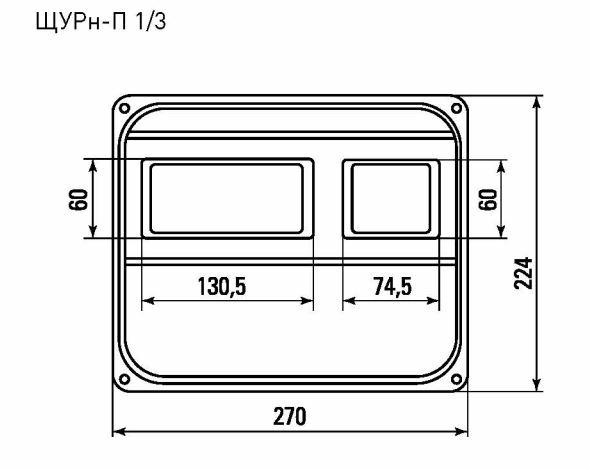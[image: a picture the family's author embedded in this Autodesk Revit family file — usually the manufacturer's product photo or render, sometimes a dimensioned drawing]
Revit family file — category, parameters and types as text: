
# Revit family: EKF_EE_ЩМПг_IP54_Basic
name_source: partatom
category: Электрооборудование
units: mm (PartAtom-declared; Revit-internal decimal feet)

## family parameters
Всегда вертикально = Да
На основе рабочей плоскости = Нет
Общий = Нет
При загрузке вырезать с полостями = Нет
Размер круглого соединителя = Использовать диаметр
Тип детали = Силовой щит
Точка расчета площади = Да

## types (5) — shared parameters
ADSK_Единица измерения = компл.
ADSK_Завод-изготовитель = EKF
ADSK_Классификация нагрузок = Прочее
ADSK_Количество = 1
ADSK_Количество фаз = 3
ADSK_Коэффициент мощности = 1
ADSK_Материал = RAL 7035_Сталь
ADSK_Напряжение = 400 В
ADSK_Номинальная мощность = 0 Вт
ADSK_Полная мощность = 0 В·А
ADSK_Ток = 125 А
Изготовитель = EKF
Серия номенклатуры = Basic
Степень защиты IP = IP54
ТВ = EKF
Тип установки = Навесной
zero-valued in all types: ADSK_Масса, Количество DIN-реек, Количество модулей на DIN-рейке, Максимальное количество модулей

## per-type parameters (varying)
| type | ADSK_Код изделия | ADSK_Марка | ADSK_Наименование | ADSK_Обозначение | ADSK_Размер_Высота | ADSK_Размер_Глубина | ADSK_Размер_Ширина | Описание | Тип |
| ЩМПг- 40.30.22 (ЩРНМ-1) IP54 EKF Basic | mb24-1-bas | ЩМПг- 40.30.22 (ЩРНМ-1) IP54 | Щит с монтажной панелью ЩМПг- 40.30.22 (ЩРНМ-1) IP54 EKF Basic | ЩМПг- 40.30.22 (ЩРНМ-1) IP54 | 400 мм | 220 мм | 300 мм | Щит с монтажной панелью ЩМПг- 40.30.22 (ЩРНМ-1) IP54 EKF Basic | 102 мм |
| ЩМПг- 50.40.22 (ЩРНМ-2) IP54 EKF Basic | mb24-2-bas | ЩМПг- 50.40.22 (ЩРНМ-2) IP54 | Щит с монтажной панелью ЩМПг- 50.40.22 (ЩРНМ-2) IP54 EKF Basic | ЩМПг- 50.40.22 (ЩРНМ-2) IP54 | 500 мм | 220 мм | 400 мм | Щит с монтажной панелью ЩМПг- 50.40.22 (ЩРНМ-2) IP54 EKF Basic | 103 мм |
| ЩМПг- 65.50.22 (ЩРНМ-3) IP54 EKF Basic | mb24-3-bas | ЩМПг- 65.50.22 (ЩРНМ-3) IP54 | Щит с монтажной панелью ЩМПг- 65.50.22 (ЩРНМ-3) IP54 EKF Basic | ЩМПг- 65.50.22 (ЩРНМ-3) IP54 | 650 мм | 220 мм | 500 мм | Щит с монтажной панелью ЩМПг- 65.50.22 (ЩРНМ-3) IP54 EKF Basic | 104 мм |
| ЩМПг- 80.60.25 (ЩРНМ-4) IP54 EKF Basic | mb24-4-bas | ЩМПг- 80.60.25 (ЩРНМ-4) IP54 | Щит с монтажной панелью ЩМПг- 80.60.25 (ЩРНМ-4) IP54 EKF Basic | ЩМПг- 80.60.25 (ЩРНМ-4) IP54 | 800 мм | 250 мм | 600 мм | Щит с монтажной панелью ЩМПг- 80.60.25 (ЩРНМ-4) IP54 EKF Basic | 105 мм |
| ЩМПг-100.65.30 (ЩРНМ-5) IP54 EKF Basic | mb24-5-bas | ЩМПг-100.65.30 (ЩРНМ-5) IP54 | Щит с монтажной панелью ЩМПг-100.65.30 (ЩРНМ-5) IP54 EKF Basic | ЩМПг-100.65.30 (ЩРНМ-5) IP54 | 1000 мм | 300 мм | 650 мм | Щит с монтажной панелью ЩМПг-100.65.30 (ЩРНМ-5) IP54 EKF Basic | 106 мм |
